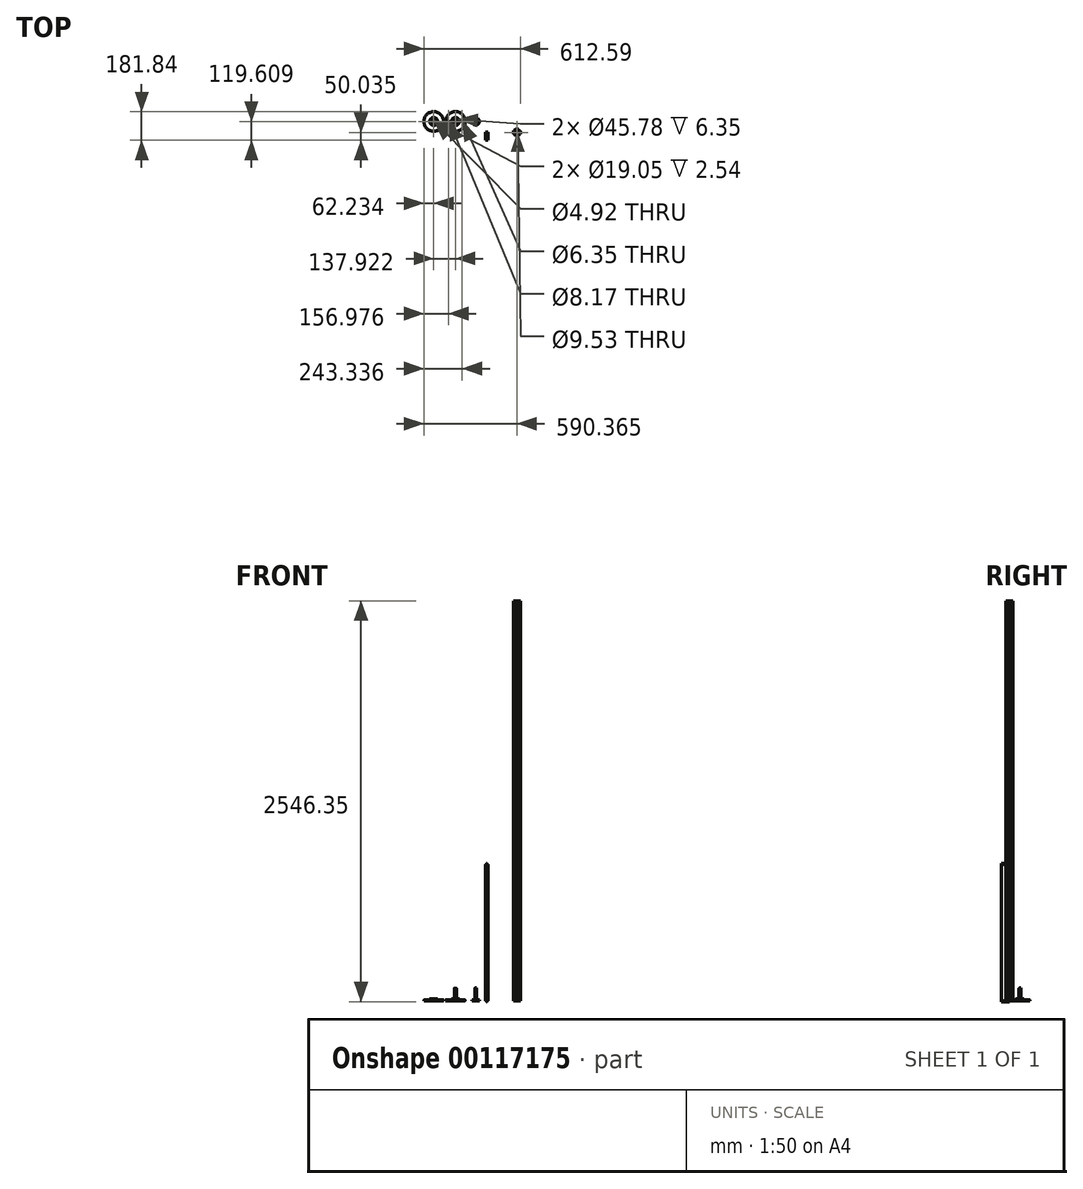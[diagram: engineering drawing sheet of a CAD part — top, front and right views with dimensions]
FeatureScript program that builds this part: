
annotation { "Feature Type Name" : "Feature", "Feature Type Description" : "" }
export const myFeature = defineFeature(function(context is Context, id is Id, definition is map)
    precondition{}
    {
        {
            var Q0;
            Q0=qCreatedBy(makeId("Top.planeOp"),FACE);
            var sketch = newSketch(context, id + "F0", { "sketchPlane" : qUnion([Q0])});
            skLineSegment(sketch, "E0.bottom", {"start": v(12.7, 0) * mm, "end": v(19.84, 0) * mm});
            skLineSegment(sketch, "E0.top", {"start": v(12.7, -44.45) * mm, "end": v(19.84, -44.45) * mm});
            skLineSegment(sketch, "E0.left", {"start": v(0, -12.7) * mm, "end": v(0, -19.84) * mm});
            skLineSegment(sketch, "E0.right", {"start": v(44.45, -12.7) * mm, "end": v(44.45, -19.84) * mm});
            skLineSegment(sketch, "E1", {"start": v(0, -22.23) * mm, "end": v(44.45, -22.23) * mm, "construction": true});
            skLineSegment(sketch, "E2", {"start": v(22.23, 0) * mm, "end": v(22.23, -44.45) * mm, "construction": true});
            skLineSegment(sketch, "E3", {"start": v(0, -12.7) * mm, "end": v(0, -19.84) * mm, "construction": true});
            skPoint(sketch, "E4", {"position": v(0, -22.23) * mm});
            skArc(sketch, "E5", {"start": v(0, -12.7) * mm, "mid": v(8.98, -8.98) * mm, "end": v(12.7, 0) * mm});
            skArc(sketch, "E6", {"start": v(31.75, 0) * mm, "mid": v(35.47, -8.98) * mm, "end": v(44.45, -12.7) * mm});
            skArc(sketch, "E7", {"start": v(44.45, -31.75) * mm, "mid": v(35.47, -35.47) * mm, "end": v(31.75, -44.45) * mm});
            skArc(sketch, "E8", {"start": v(12.7, -44.45) * mm, "mid": v(8.98, -35.47) * mm, "end": v(0, -31.75) * mm});
            skPoint(sketch, "E9", {"position": v(22.23, 0) * mm});
            skLineSegment(sketch, "E10.1.0", {"start": v(0, -24.6) * mm, "end": v(1.59, -24.6) * mm});
            skLineSegment(sketch, "E10.1.1", {"start": v(12.7, -24.6) * mm, "end": v(12.7, -19.84) * mm});
            skLineSegment(sketch, "E10.1.2", {"start": v(0, -19.84) * mm, "end": v(1.59, -19.84) * mm});
            skPoint(sketch, "E10.center", {"position": v(22.23, -22.23) * mm});
            skArc(sketch, "E11.0", {"start": v(1.59, -14.2) * mm, "mid": v(10.1, -10.1) * mm, "end": v(14.2, -1.59) * mm});
            skArc(sketch, "E12.0", {"start": v(14.2, -42.86) * mm, "mid": v(10.1, -34.35) * mm, "end": v(1.59, -30.25) * mm});
            skLineSegment(sketch, "E13.0", {"start": v(1.59, -14.2) * mm, "end": v(1.59, -19.84) * mm});
            skLineSegment(sketch, "E14", {"start": v(6.35, -12.8) * mm, "end": v(6.35, -19.84) * mm});
            skLineSegment(sketch, "E15.trimOffspring", {"start": v(6.35, -19.84) * mm, "end": v(12.7, -19.84) * mm});
            skLineSegment(sketch, "E16.trimOffspring", {"start": v(6.35, -24.6) * mm, "end": v(6.35, -31.65) * mm});
            skLineSegment(sketch, "E17.trimOffspring", {"start": v(6.35, -24.6) * mm, "end": v(12.7, -24.6) * mm});
            skLineSegment(sketch, "E18.trimOffspring", {"start": v(1.59, -24.6) * mm, "end": v(1.59, -30.25) * mm});
            skLineSegment(sketch, "E19.trimOffspring", {"start": v(0, -24.6) * mm, "end": v(0, -31.75) * mm, "construction": true});
            skLineSegment(sketch, "E20.trimOffspring", {"start": v(0, -24.6) * mm, "end": v(0, -31.75) * mm});
            skArc(sketch, "E21.1.0", {"start": v(14.2, -42.86) * mm, "mid": v(9.53, -33.8) * mm, "end": v(0, -30.16) * mm});
            skLineSegment(sketch, "E21.1.1", {"start": v(12.8, -38.1) * mm, "end": v(19.84, -38.1) * mm});
            skLineSegment(sketch, "E21.1.2", {"start": v(14.2, -42.86) * mm, "end": v(19.84, -42.86) * mm});
            skLineSegment(sketch, "E21.1.3", {"start": v(24.6, -42.86) * mm, "end": v(30.25, -42.86) * mm});
            skLineSegment(sketch, "E21.1.4", {"start": v(24.6, -44.45) * mm, "end": v(24.6, -42.86) * mm});
            skLineSegment(sketch, "E21.1.5", {"start": v(19.84, -44.45) * mm, "end": v(19.84, -42.86) * mm});
            skLineSegment(sketch, "E21.1.6", {"start": v(19.84, -38.1) * mm, "end": v(19.84, -31.75) * mm});
            skLineSegment(sketch, "E21.1.7", {"start": v(24.6, -31.75) * mm, "end": v(19.84, -31.75) * mm});
            skLineSegment(sketch, "E21.1.8", {"start": v(24.6, -38.1) * mm, "end": v(24.6, -31.75) * mm});
            skLineSegment(sketch, "E21.1.9", {"start": v(24.6, -38.1) * mm, "end": v(31.65, -38.1) * mm});
            skArc(sketch, "E21.1.10", {"start": v(42.86, -30.25) * mm, "mid": v(34.35, -34.35) * mm, "end": v(30.25, -42.86) * mm});
            skArc(sketch, "E21.2.0", {"start": v(42.86, -30.25) * mm, "mid": v(34.35, -34.35) * mm, "end": v(30.25, -42.86) * mm});
            skLineSegment(sketch, "E21.2.1", {"start": v(38.1, -31.65) * mm, "end": v(38.1, -24.6) * mm});
            skLineSegment(sketch, "E21.2.2", {"start": v(42.86, -30.25) * mm, "end": v(42.86, -24.6) * mm});
            skLineSegment(sketch, "E21.2.3", {"start": v(42.86, -19.84) * mm, "end": v(42.86, -14.2) * mm});
            skLineSegment(sketch, "E21.2.4", {"start": v(44.45, -19.84) * mm, "end": v(42.86, -19.84) * mm});
            skLineSegment(sketch, "E21.2.5", {"start": v(44.45, -24.6) * mm, "end": v(42.86, -24.6) * mm});
            skLineSegment(sketch, "E21.2.6", {"start": v(38.1, -24.6) * mm, "end": v(31.75, -24.6) * mm});
            skLineSegment(sketch, "E21.2.7", {"start": v(31.75, -19.84) * mm, "end": v(31.75, -24.6) * mm});
            skLineSegment(sketch, "E21.2.8", {"start": v(38.1, -19.84) * mm, "end": v(31.75, -19.84) * mm});
            skLineSegment(sketch, "E21.2.9", {"start": v(38.1, -19.84) * mm, "end": v(38.1, -12.8) * mm});
            skArc(sketch, "E21.2.10", {"start": v(30.25, -1.59) * mm, "mid": v(34.35, -10.1) * mm, "end": v(42.86, -14.2) * mm});
            skArc(sketch, "E21.3.0", {"start": v(30.25, -1.59) * mm, "mid": v(34.35, -10.1) * mm, "end": v(42.86, -14.2) * mm});
            skLineSegment(sketch, "E21.3.1", {"start": v(31.65, -6.35) * mm, "end": v(24.6, -6.35) * mm});
            skLineSegment(sketch, "E21.3.2", {"start": v(30.25, -1.59) * mm, "end": v(24.6, -1.59) * mm});
            skLineSegment(sketch, "E21.3.3", {"start": v(19.84, -1.59) * mm, "end": v(14.2, -1.59) * mm});
            skLineSegment(sketch, "E21.3.4", {"start": v(19.84, 0) * mm, "end": v(19.84, -1.59) * mm});
            skLineSegment(sketch, "E21.3.5", {"start": v(24.6, 0) * mm, "end": v(24.6, -1.59) * mm});
            skLineSegment(sketch, "E21.3.6", {"start": v(24.6, -6.35) * mm, "end": v(24.6, -12.7) * mm});
            skLineSegment(sketch, "E21.3.7", {"start": v(19.84, -12.7) * mm, "end": v(24.6, -12.7) * mm});
            skLineSegment(sketch, "E21.3.8", {"start": v(19.84, -6.35) * mm, "end": v(19.84, -12.7) * mm});
            skLineSegment(sketch, "E21.3.9", {"start": v(19.84, -6.35) * mm, "end": v(12.8, -6.35) * mm});
            skArc(sketch, "E21.3.10", {"start": v(0, -14.29) * mm, "mid": v(9.53, -10.65) * mm, "end": v(14.2, -1.59) * mm});
            skLineSegment(sketch, "E22.trimOffspring", {"start": v(24.6, -44.45) * mm, "end": v(31.75, -44.45) * mm});
            skPoint(sketch, "E23.orphan", {"position": v(14.29, -44.45) * mm});
            skPoint(sketch, "E24.orphan", {"position": v(30.16, -44.45) * mm});
            skLineSegment(sketch, "E25.trimOffspring", {"start": v(44.45, -24.6) * mm, "end": v(44.45, -31.75) * mm});
            skPoint(sketch, "E26.orphan", {"position": v(44.45, -30.16) * mm});
            skPoint(sketch, "E27.orphan", {"position": v(44.45, -14.29) * mm});
            skPoint(sketch, "E28.orphan", {"position": v(24.6, 0) * mm});
            skLineSegment(sketch, "E29.trimOffspring", {"start": v(24.6, 0) * mm, "end": v(31.75, 0) * mm});
            skPoint(sketch, "E30.bottom.start.orphan", {"position": v(19.84, 0) * mm});
            skPoint(sketch, "E31.orphan", {"position": v(30.16, 0) * mm});
            skPoint(sketch, "E32.orphan", {"position": v(14.29, 0) * mm});
            skSolve(sketch);
        }
        {
            var Q0;
            Q0 = qSketchRegion(id + "F0", true);
            extrude(context, id + "F1", {"entities" : qUnion([Q0]), "depth" : 2540 * mm});
        }
        {
            var Q0;
            Q0=qCreatedBy(makeId("Top.planeOp"),FACE);
            var sketch = newSketch(context, id + "F2", { "sketchPlane" : qUnion([Q0])});
            skCircle(sketch, "E33", {"center": v(-505.9, 47.35) * mm, "radius": 62.23 * mm});
            skSolve(sketch);
        }
        {
            var Q0;
            Q0 = qSketchRegion(id + "F2", true);
            extrude(context, id + "F3", {"entities" : qUnion([Q0]), "depth" : 6.35 * mm});
        }
        {
            var Q0;
            Q0=makeQuery(id+"F3.opExtrude","CAP_FACE",FACE,{"disambiguationData":[OSD([sQuery(id+"F2.wireOp",EDGE,"E33")])],"isStart":false});
            var sketch = newSketch(context, id + "F4", { "sketchPlane" : qUnion([Q0])});
            skCircle(sketch, "E34", {"center": v(-505.9, 47.35) * mm, "radius": 25.4 * mm});
            skSolve(sketch);
        }
        {
            var Q0;
            Q0 = qSketchRegion(id + "F4", true);
            extrude(context, id + "F5", {"entities" : qUnion([Q0]), "operationType" : NewBodyOperationType.ADD, "depth" : 6.35 * mm});
        }
        {
            var Q0;
            Q0=makeQuery(id+"F5.opExtrude","CAP_EDGE",EDGE,{"disambiguationData":[OSD([sQuery(id+"F4.wireOp",EDGE,"E34")])],"isStart":true});
            var Q1;
            Q1=makeQuery(id+"F3.opExtrude","CAP_EDGE",EDGE,{"disambiguationData":[OSD([sQuery(id+"F2.wireOp",EDGE,"E33")])],"isStart":false});
            fillet(context, id + "F6", {"entities" : qUnion([Q0, Q1]), "radius" : 5.08 * mm, "tangentPropagation" : true, "allowEdgeOverflow" : false});
        }
        {
            var Q0;
            Q0=makeQuery(id+"F5.opExtrude","CAP_FACE",FACE,{"disambiguationData":[OSD([sQuery(id+"F4.wireOp",EDGE,"E34")])],"isStart":false});
            var sketch = newSketch(context, id + "F7", { "sketchPlane" : qUnion([Q0])});
            skCircle(sketch, "E35", {"center": v(-505.9, 47.35) * mm, "radius": 22.89 * mm});
            skSolve(sketch);
        }
        {
            var Q0;
            Q0 = qSketchRegion(id + "F7", true);
            extrude(context, id + "F8", {"entities" : qUnion([Q0]), "operationType" : NewBodyOperationType.REMOVE, "oppositeDirection" : true, "depth" : 6.35 * mm});
        }
        {
            var Q0;
            Q0=makeQuery(id+"F8.boolean.opBoolean","COPY",FACE,{"derivedFrom":makeQuery(id+"F8.opExtrude","CAP_FACE",FACE,{"disambiguationData":[OSD([sQuery(id+"F7.wireOp",EDGE,"E35")])],"isStart":false})});
            var sketch = newSketch(context, id + "F9", { "sketchPlane" : qUnion([Q0])});
            skCircle(sketch, "E36", {"center": v(-505.9, 47.35) * mm, "radius": 9.53 * mm});
            skSolve(sketch);
        }
        {
            var Q0;
            Q0 = qSketchRegion(id + "F9", true);
            extrude(context, id + "F10", {"entities" : qUnion([Q0]), "operationType" : NewBodyOperationType.REMOVE, "oppositeDirection" : true, "depth" : 2.54 * mm});
        }
        {
            var Q0;
            Q0=makeQuery(id+"F10.boolean.opBoolean","COPY",FACE,{"derivedFrom":makeQuery(id+"F10.opExtrude","CAP_FACE",FACE,{"disambiguationData":[OSD([sQuery(id+"F9.wireOp",EDGE,"E36")])],"isStart":false})});
            var sketch = newSketch(context, id + "F11", { "sketchPlane" : qUnion([Q0])});
            skCircle(sketch, "E37", {"center": v(-505.9, 47.35) * mm, "radius": 2.46 * mm});
            skSolve(sketch);
        }
        {
            var Q0;
            Q0 = qSketchRegion(id + "F11", true);
            extrude(context, id + "F12", {"entities" : qUnion([Q0]), "operationType" : NewBodyOperationType.REMOVE, "oppositeDirection" : true, "depth" : 25.4 * mm});
        }
        {
            var Q0;
            Q0=makeQuery(id+"F3.opExtrude","SWEPT_BODY",BODY,{"disambiguationData":[OSD([sQuery(id+"F2.wireOp",EDGE,"E33")])]});
            transform(context, id + "F13", {"entities" : qUnion([Q0]), "transformType" : TransformType.TRANSLATION_3D, "dx" : 137.92 * mm, "dy" : 0 * mm, "dz" : 0 * mm, "makeCopy" : true});
        }
        {
            var Q0;
            Q0=makeQuery(id+"F13.opPattern","COPY",FACE,{"derivedFrom":makeQuery(id+"F3.opExtrude","CAP_FACE",FACE,{"disambiguationData":[OSD([sQuery(id+"F2.wireOp",EDGE,"E33")])],"isStart":false}),"instanceName":"1"});
            var sketch = newSketch(context, id + "F14", { "sketchPlane" : qUnion([Q0])});
            skLineSegment(sketch, "E38", {"start": v(-367.98, 47.35) * mm, "end": v(-425.13, 47.35) * mm, "construction": true});
            skLineSegment(sketch, "E39", {"start": v(-425.13, 47.35) * mm, "end": v(-310.83, 47.35) * mm, "construction": true});
            skCircle(sketch, "E40", {"center": v(-411.16, 47.35) * mm, "radius": 4.09 * mm});
            skCircle(sketch, "E41", {"center": v(-324.8, 47.35) * mm, "radius": 3.18 * mm});
            skSolve(sketch);
        }
        {
            var Q0;
            Q0 = qSketchRegion(id + "F14", true);
            extrude(context, id + "F15", {"entities" : qUnion([Q0]), "operationType" : NewBodyOperationType.REMOVE, "oppositeDirection" : true, "depth" : 25.4 * mm});
        }
        {
            var Q0;
            Q0=qCreatedBy(makeId("Top.planeOp"),FACE);
            var sketch = newSketch(context, id + "F16", { "sketchPlane" : qUnion([Q0])});
            skCircle(sketch, "E42", {"center": v(-238.79, 47.55) * mm, "radius": 22.89 * mm});
            skSolve(sketch);
        }
        {
            var Q0;
            Q0 = qSketchRegion(id + "F16", true);
            extrude(context, id + "F17", {"entities" : qUnion([Q0]), "depth" : 6.35 * mm});
        }
        {
            var Q0;
            Q0=makeQuery(id+"F17.opExtrude","CAP_FACE",FACE,{"disambiguationData":[OSD([sQuery(id+"F16.wireOp",EDGE,"E42")])],"isStart":false});
            var sketch = newSketch(context, id + "F18", { "sketchPlane" : qUnion([Q0])});
            skArc(sketch, "E43", {"start": v(-247.2, 38.04) * mm, "mid": v(-238.79, 34.85) * mm, "end": v(-230.36, 38.04) * mm});
            skLineSegment(sketch, "E44", {"start": v(-247.2, 57.06) * mm, "end": v(-247.2, 38.04) * mm});
            skLineSegment(sketch, "E45", {"start": v(-230.36, 57.06) * mm, "end": v(-230.36, 38.04) * mm});
            skArc(sketch, "E46.trimOffspring", {"start": v(-230.36, 57.06) * mm, "mid": v(-238.79, 60.25) * mm, "end": v(-247.2, 57.06) * mm});
            skSolve(sketch);
        }
        {
            var Q0;
            Q0 = qSketchRegion(id + "F18", true);
            extrude(context, id + "F19", {"entities" : qUnion([Q0]), "operationType" : NewBodyOperationType.ADD, "depth" : 6.35 * mm});
        }
        {
            var Q0;
            Q0=makeQuery(id+"F19.opExtrude","CAP_FACE",FACE,{"disambiguationData":[OSD([sQuery(id+"F18.wireOp",EDGE,"E43"),sQuery(id+"F18.wireOp",EDGE,"E44"),sQuery(id+"F18.wireOp",EDGE,"E45"),sQuery(id+"F18.wireOp",EDGE,"E46.trimOffspring")])],"isStart":false});
            var sketch = newSketch(context, id + "F20", { "sketchPlane" : qUnion([Q0])});
            skCircle(sketch, "E47", {"center": v(-238.79, 47.55) * mm, "radius": 4.76 * mm});
            skSolve(sketch);
        }
        {
            var Q0;
            Q0 = qSketchRegion(id + "F20", true);
            extrude(context, id + "F21", {"entities" : qUnion([Q0]), "operationType" : NewBodyOperationType.ADD, "depth" : 69.85 * mm});
        }
        {
            var Q0;
            Q0=makeQuery(id+"F1.opExtrude","CAP_FACE",FACE,{"disambiguationData":[OSD([sQuery(id+"F0.wireOp",EDGE,"E0.bottom"),sQuery(id+"F0.wireOp",EDGE,"E0.top"),sQuery(id+"F0.wireOp",EDGE,"E0.left"),sQuery(id+"F0.wireOp",EDGE,"E0.right"),sQuery(id+"F0.wireOp",EDGE,"E5"),sQuery(id+"F0.wireOp",EDGE,"E6"),sQuery(id+"F0.wireOp",EDGE,"E7"),sQuery(id+"F0.wireOp",EDGE,"E8"),sQuery(id+"F0.wireOp",EDGE,"E10.1.0"),sQuery(id+"F0.wireOp",EDGE,"E10.1.1"),sQuery(id+"F0.wireOp",EDGE,"E10.1.2"),sQuery(id+"F0.wireOp",EDGE,"E13.0"),sQuery(id+"F0.wireOp",EDGE,"E14"),sQuery(id+"F0.wireOp",EDGE,"E15.trimOffspring"),sQuery(id+"F0.wireOp",EDGE,"E16.trimOffspring"),sQuery(id+"F0.wireOp",EDGE,"E17.trimOffspring"),sQuery(id+"F0.wireOp",EDGE,"E18.trimOffspring"),sQuery(id+"F0.wireOp",EDGE,"E20.trimOffspring"),sQuery(id+"F0.wireOp",EDGE,"E21.1.0"),sQuery(id+"F0.wireOp",EDGE,"E21.1.1"),sQuery(id+"F0.wireOp",EDGE,"E21.1.2"),sQuery(id+"F0.wireOp",EDGE,"E21.1.3"),sQuery(id+"F0.wireOp",EDGE,"E21.1.4"),sQuery(id+"F0.wireOp",EDGE,"E21.1.5"),sQuery(id+"F0.wireOp",EDGE,"E21.1.6"),sQuery(id+"F0.wireOp",EDGE,"E21.1.7"),sQuery(id+"F0.wireOp",EDGE,"E21.1.8"),sQuery(id+"F0.wireOp",EDGE,"E21.1.9"),sQuery(id+"F0.wireOp",EDGE,"E21.2.0"),sQuery(id+"F0.wireOp",EDGE,"E21.2.1"),sQuery(id+"F0.wireOp",EDGE,"E21.2.2"),sQuery(id+"F0.wireOp",EDGE,"E21.2.3"),sQuery(id+"F0.wireOp",EDGE,"E21.2.4"),sQuery(id+"F0.wireOp",EDGE,"E21.2.5"),sQuery(id+"F0.wireOp",EDGE,"E21.2.6"),sQuery(id+"F0.wireOp",EDGE,"E21.2.7"),sQuery(id+"F0.wireOp",EDGE,"E21.2.8"),sQuery(id+"F0.wireOp",EDGE,"E21.2.9"),sQuery(id+"F0.wireOp",EDGE,"E21.3.0"),sQuery(id+"F0.wireOp",EDGE,"E21.3.1"),sQuery(id+"F0.wireOp",EDGE,"E21.3.2"),sQuery(id+"F0.wireOp",EDGE,"E21.3.3"),sQuery(id+"F0.wireOp",EDGE,"E21.3.4"),sQuery(id+"F0.wireOp",EDGE,"E21.3.5"),sQuery(id+"F0.wireOp",EDGE,"E21.3.6"),sQuery(id+"F0.wireOp",EDGE,"E21.3.7"),sQuery(id+"F0.wireOp",EDGE,"E21.3.8"),sQuery(id+"F0.wireOp",EDGE,"E21.3.9"),sQuery(id+"F0.wireOp",EDGE,"E21.3.10"),sQuery(id+"F0.wireOp",EDGE,"E22.trimOffspring"),sQuery(id+"F0.wireOp",EDGE,"E25.trimOffspring"),sQuery(id+"F0.wireOp",EDGE,"E29.trimOffspring")])],"isStart":true});
            var sketch = newSketch(context, id + "F22", { "sketchPlane" : qUnion([Q0])});
            skCircle(sketch, "E48", {"center": v(22.22, 22.23) * mm, "radius": 4.76 * mm});
            skPoint(sketch, "E48.centerSnap0", {"position": v(12.7, 22.23) * mm});
            skPoint(sketch, "E48.centerSnap1", {"position": v(22.22, 12.7) * mm});
            skSolve(sketch);
        }
        {
            var Q0;
            Q0 = qSketchRegion(id + "F22", true);
            extrude(context, id + "F23", {"entities" : qUnion([Q0]), "operationType" : NewBodyOperationType.REMOVE, "endBound" : BoundingType.THROUGH_ALL, "oppositeDirection" : true, "depth" : 25.4 * mm});
        }
        {
            var Q0;
            Q0=makeQuery(id+"F13.opPattern","COPY",FACE,{"derivedFrom":makeQuery(id+"F3.opExtrude","CAP_FACE",FACE,{"disambiguationData":[OSD([sQuery(id+"F2.wireOp",EDGE,"E33")])],"isStart":true}),"instanceName":"1"});
            var sketch = newSketch(context, id + "F24", { "sketchPlane" : qUnion([Q0])});
            skCircle(sketch, "E49.0", {"center": v(-367.98, -47.35) * mm, "radius": 2.46 * mm});
            skSolve(sketch);
        }
        {
            var Q0;
            Q0 = qSketchRegion(id + "F24", true);
            extrude(context, id + "F25", {"entities" : qUnion([Q0]), "operationType" : NewBodyOperationType.ADD, "oppositeDirection" : true, "depth" : 25.4 * mm});
        }
        {
            var Q0;
            Q0=makeQuery(id+"F25.opExtrude","CAP_FACE",FACE,{"disambiguationData":[OSD([sQuery(id+"F24.wireOp",EDGE,"E49.0")])],"isStart":false});
            var sketch = newSketch(context, id + "F26", { "sketchPlane" : qUnion([Q0])});
            skCircle(sketch, "E50", {"center": v(-367.98, 47.35) * mm, "radius": 6.35 * mm});
            skSolve(sketch);
        }
        {
            var Q0;
            Q0 = qSketchRegion(id + "F26", true);
            extrude(context, id + "F27", {"entities" : qUnion([Q0]), "operationType" : NewBodyOperationType.ADD, "depth" : 47.62 * mm});
        }
        {
            var Q0;
            Q0=makeQuery(id+"F27.opExtrude","CAP_FACE",FACE,{"disambiguationData":[OSD([sQuery(id+"F26.wireOp",EDGE,"E50")])],"isStart":false});
            var sketch = newSketch(context, id + "F28", { "sketchPlane" : qUnion([Q0])});
            skCircle(sketch, "E51", {"center": v(-367.98, 47.35) * mm, "radius": 3.18 * mm});
            skSolve(sketch);
        }
        {
            var Q0;
            Q0 = qSketchRegion(id + "F28", true);
            extrude(context, id + "F29", {"entities" : qUnion([Q0]), "operationType" : NewBodyOperationType.ADD, "depth" : 3.17 * mm});
        }
        {
            var Q0;
            Q0=makeQuery(id+"F29.opExtrude","CAP_FACE",FACE,{"disambiguationData":[OSD([sQuery(id+"F28.wireOp",EDGE,"E51")])],"isStart":false});
            var sketch = newSketch(context, id + "F30", { "sketchPlane" : qUnion([Q0])});
            skCircle(sketch, "E52.0", {"center": v(-367.98, 47.35) * mm, "radius": 6.35 * mm});
            skSolve(sketch);
        }
        {
            var Q0;
            Q0 = qSketchRegion(id + "F30", true);
            extrude(context, id + "F31", {"entities" : qUnion([Q0]), "operationType" : NewBodyOperationType.ADD, "depth" : 3.17 * mm});
        }
        {
            var Q0;
            Q0=qCreatedBy(makeId("Top.planeOp"),FACE);
            var sketch = newSketch(context, id + "F32", { "sketchPlane" : qUnion([Q0])});
            skLineSegment(sketch, "E53.bottom", {"start": v(-176.65, -21.46) * mm, "end": v(-160.77, -21.46) * mm});
            skLineSegment(sketch, "E53.top", {"start": v(-176.65, -72.26) * mm, "end": v(-160.77, -72.26) * mm});
            skLineSegment(sketch, "E53.left", {"start": v(-176.65, -21.46) * mm, "end": v(-176.65, -72.26) * mm});
            skLineSegment(sketch, "E53.right", {"start": v(-160.77, -21.46) * mm, "end": v(-160.77, -72.26) * mm});
            skSolve(sketch);
        }
        {
            var Q0;
            Q0 = qSketchRegion(id + "F32", true);
            extrude(context, id + "F33", {"entities" : qUnion([Q0]), "depth" : 866.77 * mm});
        }
        {
            var Q0;
            Q0=makeQuery(id+"F33.opExtrude","CAP_FACE",FACE,{"disambiguationData":[OSD([sQuery(id+"F32.wireOp",EDGE,"E53.bottom"),sQuery(id+"F32.wireOp",EDGE,"E53.top"),sQuery(id+"F32.wireOp",EDGE,"E53.left"),sQuery(id+"F32.wireOp",EDGE,"E53.right")])],"isStart":false});
            var sketch = newSketch(context, id + "F34", { "sketchPlane" : qUnion([Q0])});
            skLineSegment(sketch, "E54.bottom", {"start": v(-171.1, -21.46) * mm, "end": v(-166.33, -21.46) * mm});
            skLineSegment(sketch, "E54.top", {"start": v(-171.1, -72.26) * mm, "end": v(-166.33, -72.26) * mm});
            skLineSegment(sketch, "E54.left", {"start": v(-171.1, -21.46) * mm, "end": v(-171.1, -72.26) * mm});
            skLineSegment(sketch, "E54.right", {"start": v(-166.33, -21.46) * mm, "end": v(-166.33, -72.26) * mm});
            skLineSegment(sketch, "E55", {"start": v(-168.7, -21.46) * mm, "end": v(-168.7, -72.26) * mm, "construction": true});
            skPoint(sketch, "E56", {"position": v(-168.7, -21.46) * mm});
            skSolve(sketch);
        }
        {
            var Q0;
            Q0 = qSketchRegion(id + "F34", true);
            extrude(context, id + "F35", {"entities" : qUnion([Q0]), "operationType" : NewBodyOperationType.ADD, "depth" : 6.35 * mm, "hasSecondDirection" : true, "secondDirectionOppositeDirection" : true, "secondDirectionDepth" : 873.12 * mm});
        }
        {
            var Q0;
            Q0=qCreatedBy(makeId("Top.planeOp"),FACE);
            var sketch = newSketch(context, id + "F36", { "sketchPlane" : qUnion([Q0])});
            skLineSegment(sketch, "E57.0", {"start": v(-160.77, -21.46) * mm, "end": v(-160.77, -72.26) * mm});
            skLineSegment(sketch, "E57.1", {"start": v(-176.65, -21.46) * mm, "end": v(-176.65, -72.26) * mm});
            skSolve(sketch);
        }
        {
            var Q0;
            Q0=qCreatedBy(makeId("Top.planeOp"),FACE);
            var sketch = newSketch(context, id + "F37", { "sketchPlane" : qUnion([Q0])});
            skLineSegment(sketch, "E58.0", {"start": v(-176.65, -21.46) * mm, "end": v(-176.65, -72.26) * mm});
            skLineSegment(sketch, "E58.1", {"start": v(-160.77, -21.46) * mm, "end": v(-160.77, -72.26) * mm});
            skLineSegment(sketch, "E59", {"start": v(-176.65, -21.46) * mm, "end": v(-160.77, -21.46) * mm});
            skLineSegment(sketch, "E60", {"start": v(-176.65, -72.26) * mm, "end": v(-160.77, -72.26) * mm});
            skSolve(sketch);
        }
        {
            var Q0;
            Q0 = qSketchRegion(id + "F37", true);
            extrude(context, id + "F38", {"entities" : qUnion([Q0]), "depth" : 622.3 * mm});
        }
        {
            var Q0;
            Q0=makeQuery(id+"F38.opExtrude","CAP_FACE",FACE,{"disambiguationData":[OSD([sQuery(id+"F37.wireOp",EDGE,"E58.0"),sQuery(id+"F37.wireOp",EDGE,"E58.1"),sQuery(id+"F37.wireOp",EDGE,"E59"),sQuery(id+"F37.wireOp",EDGE,"E60")])],"isStart":false});
            var sketch = newSketch(context, id + "F39", { "sketchPlane" : qUnion([Q0])});
            skLineSegment(sketch, "E61.0", {"start": v(-171.1, -21.46) * mm, "end": v(-171.1, -72.26) * mm});
            skLineSegment(sketch, "E61.1", {"start": v(-166.33, -21.46) * mm, "end": v(-166.33, -72.26) * mm});
            skLineSegment(sketch, "E61.2", {"start": v(-171.1, -72.26) * mm, "end": v(-166.33, -72.26) * mm});
            skLineSegment(sketch, "E61.3", {"start": v(-171.1, -21.46) * mm, "end": v(-166.33, -21.46) * mm});
            skSolve(sketch);
        }
        {
            var Q0;
            Q0 = qSketchRegion(id + "F39", true);
            extrude(context, id + "F40", {"entities" : qUnion([Q0]), "operationType" : NewBodyOperationType.ADD, "depth" : 6.35 * mm, "hasSecondDirection" : true, "secondDirectionOppositeDirection" : true, "secondDirectionDepth" : 628.65 * mm});
        }
    });
